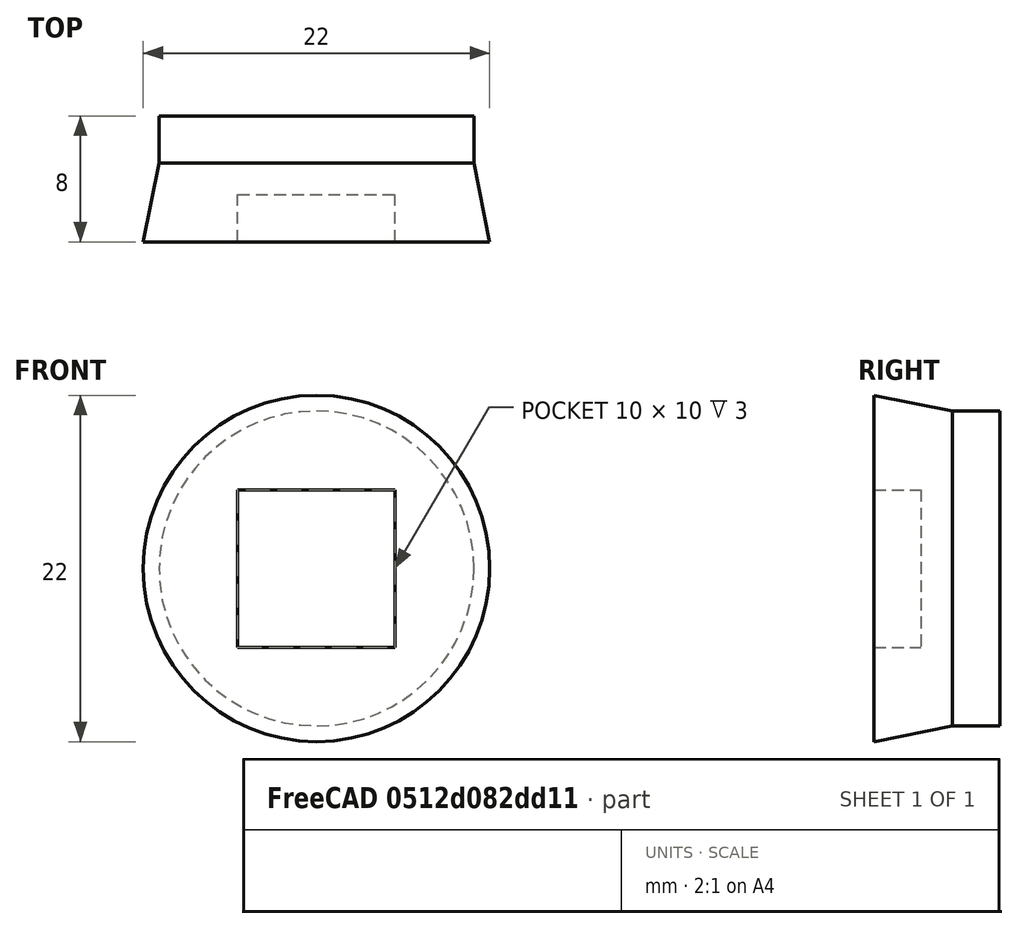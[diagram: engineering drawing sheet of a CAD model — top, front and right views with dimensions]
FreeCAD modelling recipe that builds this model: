
FCSTD DOCUMENT  (FreeCAD 1.0R39109 (Git))
Label: button
License: All rights reserved
LicenseURL: https://en.wikipedia.org/wiki/All_rights_reserved
objects: Sketcher::SketchObject×2, Mesh::Feature×2, PartDesign::Revolution×1, PartDesign::Pocket×1, PartDesign::Body×1, Spreadsheet::Sheet×1
note: 11 computed .brp shape members not serialized (recipe doc carries the construction recipe); baked Part::Feature solids carry a one-line shape summary decoded from their .brp
EXTERNAL_REF file=mount_stud.FCStd obj=Spreadsheet002

FEATURE [Sketcher::SketchObject] Sketch018
  ArcFitTolerance = 1e-06
  AttachmentSupport = -> [XY_Plane008]
  FullyConstrained = true
  MakeInternals = false
  MapMode = 5
  expr: Constraints[11] = <<ButtonSS>>.flange_height + <<ButtonSS>>.barrel_height
  expr: Constraints[12] = <<ButtonSS>>.flange_radius
  expr: Constraints[13] = <<ButtonSS>>.barrel_height
  expr: Constraints[14] = <<ButtonSS>>.radius
  expr: Constraints[15] = <<ButtonSS>>.flange_height
  sketch-geometry (6):
    g0: LineSegment StartX=0 StartY=0 StartZ=0 EndX=0 EndY=8 EndZ=0
    g1: LineSegment StartX=0 StartY=8 StartZ=0 EndX=10 EndY=8 EndZ=0
    g2: LineSegment StartX=10 StartY=8 StartZ=0 EndX=10 EndY=5 EndZ=0
    g3: LineSegment StartX=10 StartY=5 StartZ=0 EndX=11 EndY=7.1e-15 EndZ=0
    g4: LineSegment StartX=11 StartY=7.1e-15 StartZ=0 EndX=11 EndY=0 EndZ=0
    g5: LineSegment StartX=11 StartY=0 StartZ=0 EndX=0 EndY=0 EndZ=0
  constraints (17):
    c: Coincident(g-1,g0)
    c: PointOnObject(g0,g-2)
    c: Coincident(g0,g1)
    c: Coincident(g1,g2)
    c: Vertical(g2)
    c: Coincident(g2,g3)
    c: Coincident(g3,g4)
    c: PointOnObject(g4,g-1)
    c: Vertical(g4)
    c: Coincident(g4,g5)
    c: Coincident(g5,g0)
    c: Distance(g0) = 8
    c: Distance(g5) = 11
    c: Distance(g2) = 3
    c: DistanceX(g0,g1) = 10
    c: DistanceY(g3,g2) = 5
    c: Angle(g1,g2) = 1.5708
FEATURE [PartDesign::Revolution] Revolution
  Angle = 360
  Angle2 = 60
  Axis = (0,1,0)
  Base = (0,0,0)
  Profile = -> Sketch018
  ReferenceAxis = -> Sketch018 [V_Axis]
  Refine = true
  Reversed = true
  Suppressed = false
  Type = 0
FEATURE [Sketcher::SketchObject] Sketch019
  ArcFitTolerance = 1e-06
  AttachmentSupport = -> [XZ_Plane008]
  FullyConstrained = true
  MakeInternals = false
  MapMode = 5
  Placement = pos=(0,0,0) rot=(1,0,0;1.5708rad)
  expr: Constraints[10] = <<ButtonSS>>.mount_width
  expr: Constraints[11] = <<ButtonSS>>.mount_width
  expr: Constraints[8] = <<ButtonSS>>.mount_width / 2
  expr: Constraints[9] = <<ButtonSS>>.mount_width / 2
  sketch-geometry (4):
    g0: LineSegment StartX=-5 StartY=5 StartZ=0 EndX=-5 EndY=-5 EndZ=0
    g1: LineSegment StartX=-5 StartY=-5 StartZ=0 EndX=5 EndY=-5 EndZ=0
    g2: LineSegment StartX=5 StartY=-5 StartZ=0 EndX=5 EndY=5 EndZ=0
    g3: LineSegment StartX=5 StartY=5 StartZ=0 EndX=-5 EndY=5 EndZ=0
  constraints (12):
    c: Coincident(g0,g1)
    c: Coincident(g1,g2)
    c: Coincident(g2,g3)
    c: Coincident(g3,g0)
    c: Vertical(g0)
    c: Vertical(g2)
    c: Horizontal(g1)
    c: Horizontal(g3)
    c: Distance(g-1,g2) = 5
    c: Distance(g-1,g3) = 5
    c: Distance(g1) = 10
    c: Distance(g0) = 10
FEATURE [PartDesign::Pocket] Pocket006
  BaseFeature = -> Revolution
  Direction = (0,1,-2e-16)
  Length = 3
  Length2 = 5
  Profile = -> Sketch019
  ReferenceAxis = -> Sketch019 [N_Axis]
  Refine = true
  Suppressed = false
  Type = 0
  expr: Length = <<ButtonSS>>.mount_depth
FEATURE [PartDesign::Body] Body006  label="Button Body"
  AllowCompound = false
  Group = -> [Sketch018,Revolution,Sketch019,Pocket006]
  Origin = -> Origin008
  Tip = -> Pocket006
FEATURE [Spreadsheet::Sheet] Spreadsheet005  label="ButtonSS"
  cells = A1='Diameter; B1(diameter)==2 cm; A2='Barrel Height; B2(barrel_height)==3 mm; A3='Flange Height; B3(flange_height)==<<mount_stud>>#<<MountStudSS>>.height - 5 mm; A4='Flange Diameter Factor; B4(flange_factor)=1.1; A5='Flange Diameter; B5(flange_diameter)==diameter * flange_factor; A6='Mount Width; B6(mount_width)==10 mm; A7='Flange Transition Height; B7(flange_transition_height)==3 mm; A8='Total height; B8(total_height)==barrel_height + flange_height; A9='Radius; B9(radius)==diameter / 2; A10='Flange Radius; B10(flange_radius)==flange_diameter / 2; A11='Mount Depth; B11(mount_depth)==3 mm
FEATURE [Mesh::Feature] Mesh  label="Pocket006 (Meshed)"
FEATURE [Mesh::Feature] Mesh001  label="Pocket006 (Meshed)001"
